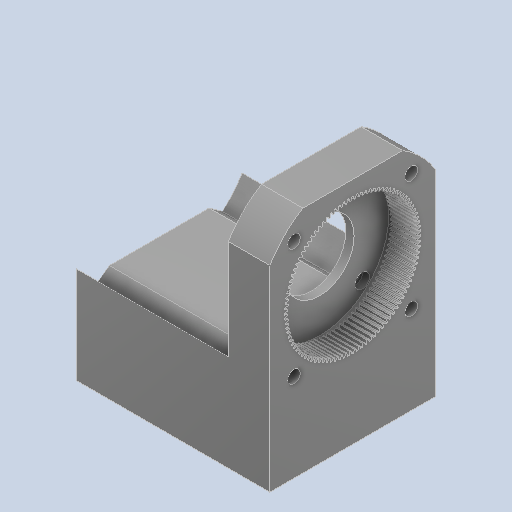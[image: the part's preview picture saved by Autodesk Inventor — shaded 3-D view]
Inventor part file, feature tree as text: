
AUTODESK INVENTOR PART (.ipt)
format: ipt  version: 2022 (Build 260153000, 153)  size: 648,704 bytes
history: mixed  units: in
note: dims shown in document units (in); Inventor stores cm internally (conversion verified against a paired STEP export)
features: extrude x6, sketch x6, plane x1, other x1, imported_body x1
ambient origin geometry x8: Origin, YZ Plane, XZ Plane, XY Plane, X Axis, Y Axis, Z Axis, Center Point
bodies: Solid1 (imported_parasolid)
feature tree (15):
  extrude  "Extrusion1"  Depth=0.3937in TaperAngle=0.0deg
  plane  "Work Plane1"
  extrude  "Extrusion2"  Depth=0.9843in TaperAngle=0.0deg
  extrude  "Extrusion5"  TaperAngle=0.0deg  [1 undecoded]
  extrude  "Extrusion6"  Depth=0.5906in TaperAngle=0.0deg
  extrude  "Extrusion7"  Depth=0.0197in
  extrude  "Extrusion8"  [1 undecoded]
  sketch  "Sketch2"  dims[d1=0.3937in d2=0.0in d3=0.3937in d4=0.0in]
  sketch  "Sketch3"  dims[d9=0.2756in d10=0.9843in d11=0.0in]
  sketch  "Sketch6"  dims[d12=0.7874in d13=0.0in d14=0.0in]
  sketch  "Sketch7"  dims[d15=0.5906in d16=0.0in d17=1.1811in d18=0.0in]
  sketch  "Sketch8"  dims[d7=0.0197in d8=0.0344in]
  sketch  "Sketch9"
  other  "96_Teeth_Gear.STEP"
  imported_body  NMx_Import_Brep_tag  [imported B-rep: ~418 faces, bbox_mm=[70.0, 83.027756, 60.0]]
note: 2 required parameter values undecoded (feature->parameter linkage not recoverable at this tier; creation-order binding heuristic only, values carry confidence <= 0.55)
